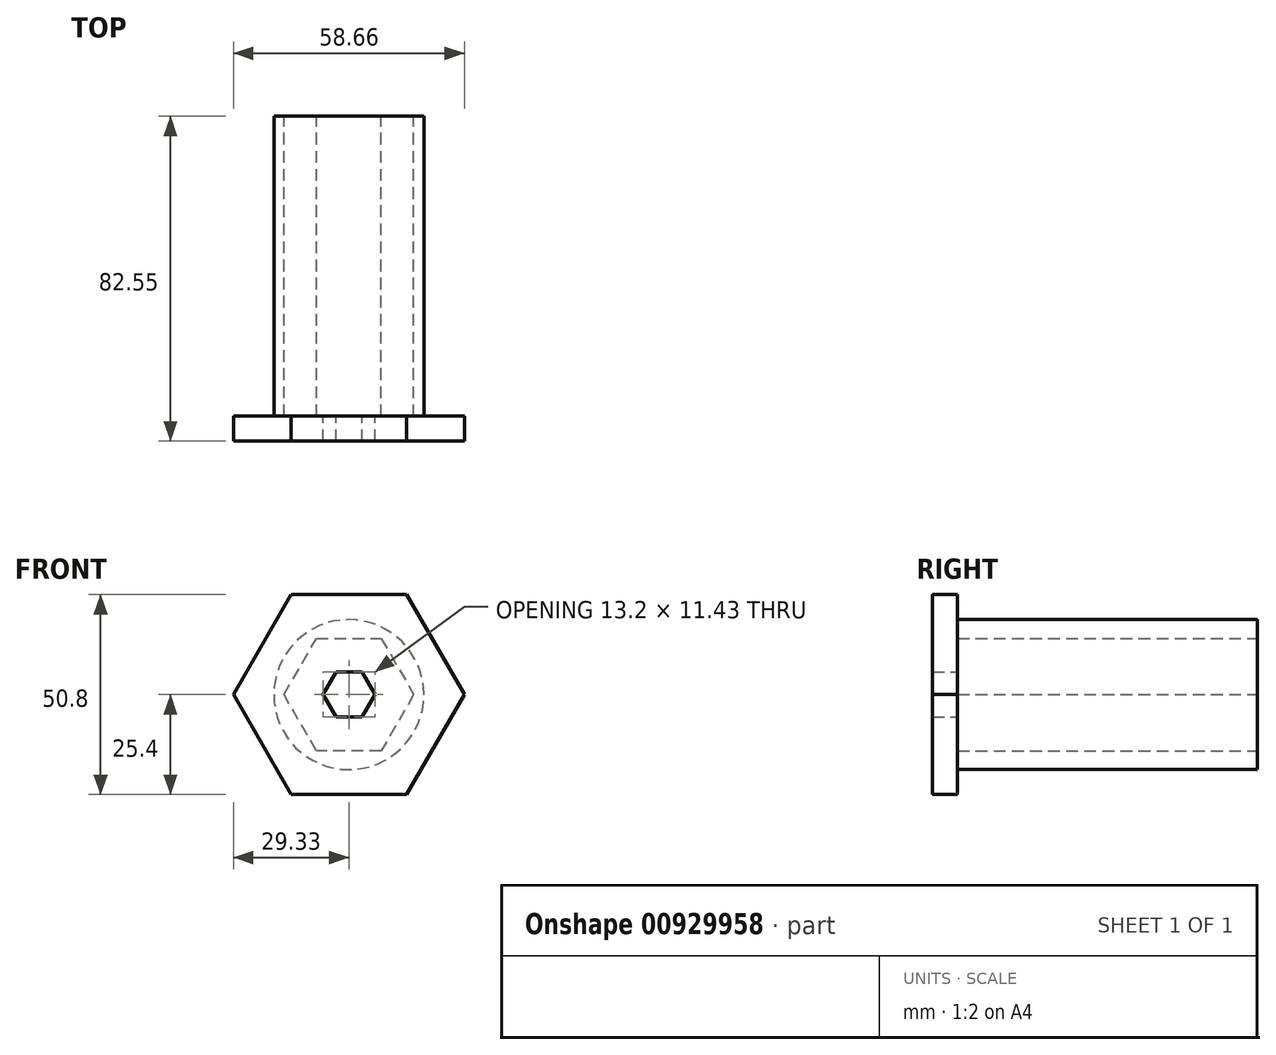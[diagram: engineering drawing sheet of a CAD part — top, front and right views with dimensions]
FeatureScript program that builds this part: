
annotation { "Feature Type Name" : "Feature", "Feature Type Description" : "" }
export const myFeature = defineFeature(function(context is Context, id is Id, definition is map)
    precondition{}
    {
        {
            var Q0;
            Q0=qCreatedBy(makeId("Front.planeOp"),FACE);
            var sketch = newSketch(context, id + "F0", { "sketchPlane" : qUnion([Q0])});
            skCircle(sketch, "E0", {"center": v(0, 0) * mm, "radius": 19.05 * mm});
            skCircle(sketch, "E1.cCircle", {"center": v(0, 0) * mm, "radius": 14.29 * mm, "construction": true});
            skLineSegment(sketch, "E1.0", {"start": v(-8.25, 14.29) * mm, "end": v(8.25, 14.29) * mm});
            skLineSegment(sketch, "E1.1", {"start": v(8.25, 14.29) * mm, "end": v(16.5, 0) * mm});
            skLineSegment(sketch, "E1.2", {"start": v(16.5, 0) * mm, "end": v(8.25, -14.29) * mm});
            skLineSegment(sketch, "E1.3", {"start": v(8.25, -14.29) * mm, "end": v(-8.25, -14.29) * mm});
            skLineSegment(sketch, "E1.4", {"start": v(-8.25, -14.29) * mm, "end": v(-16.5, 0) * mm});
            skLineSegment(sketch, "E1.5", {"start": v(-16.5, 0) * mm, "end": v(-8.25, 14.29) * mm});
            skPoint(sketch, "E1.0.midPoint", {"position": v(0, 14.29) * mm});
            skSolve(sketch);
        }
        {
            var Q0;
            Q0=makeQuery(id+"F0.imprint","IMPRINT",FACE,{"disambiguationData":[TD([[makeQuery(id+"F0.imprint","IMPRINT",EDGE,{"derivedFrom":sQuery(id+"F0.wireOp",EDGE,"E0")}),1.0]])]});
            extrude(context, id + "F1", {"entities" : qUnion([Q0]), "endBound" : BoundingType.SYMMETRIC, "depth" : 76.2 * mm, "offsetDistance" : 25.4 * mm});
        }
        {
            var Q0;
            Q0=makeQuery(id+"F1.opExtrude","CAP_FACE",FACE,{"disambiguationData":[OSD([sQuery(id+"F0.wireOp",EDGE,"E0"),sQuery(id+"F0.wireOp",EDGE,"E1.0"),sQuery(id+"F0.wireOp",EDGE,"E1.1"),sQuery(id+"F0.wireOp",EDGE,"E1.2"),sQuery(id+"F0.wireOp",EDGE,"E1.3"),sQuery(id+"F0.wireOp",EDGE,"E1.4"),sQuery(id+"F0.wireOp",EDGE,"E1.5")])],"isStart":false});
            var sketch = newSketch(context, id + "F2", { "sketchPlane" : qUnion([Q0])});
            skCircle(sketch, "E2.cCircle", {"center": v(0, 0) * mm, "radius": 25.4 * mm, "construction": true});
            skLineSegment(sketch, "E2.0", {"start": v(-14.66, 25.4) * mm, "end": v(14.66, 25.4) * mm});
            skLineSegment(sketch, "E2.1", {"start": v(14.66, 25.4) * mm, "end": v(29.33, 0) * mm});
            skLineSegment(sketch, "E2.2", {"start": v(29.33, 0) * mm, "end": v(14.66, -25.4) * mm});
            skLineSegment(sketch, "E2.3", {"start": v(14.66, -25.4) * mm, "end": v(-14.66, -25.4) * mm});
            skLineSegment(sketch, "E2.4", {"start": v(-14.66, -25.4) * mm, "end": v(-29.33, 0) * mm});
            skLineSegment(sketch, "E2.5", {"start": v(-29.33, 0) * mm, "end": v(-14.66, 25.4) * mm});
            skCircle(sketch, "E3.cCircle", {"center": v(0, 0) * mm, "radius": 5.72 * mm, "construction": true});
            skLineSegment(sketch, "E3.0", {"start": v(-3.3, 5.72) * mm, "end": v(3.3, 5.72) * mm});
            skLineSegment(sketch, "E3.1", {"start": v(3.3, 5.72) * mm, "end": v(6.6, 0) * mm});
            skLineSegment(sketch, "E3.2", {"start": v(6.6, 0) * mm, "end": v(3.3, -5.72) * mm});
            skLineSegment(sketch, "E3.3", {"start": v(3.3, -5.71) * mm, "end": v(-3.3, -5.72) * mm});
            skLineSegment(sketch, "E3.4", {"start": v(-3.3, -5.72) * mm, "end": v(-6.6, 0) * mm});
            skLineSegment(sketch, "E3.5", {"start": v(-6.6, 0) * mm, "end": v(-3.3, 5.72) * mm});
            skSolve(sketch);
        }
        {
            var Q0;
            Q0 = qSketchRegion(id + "F2", true);
            extrude(context, id + "F3", {"entities" : qUnion([Q0]), "operationType" : NewBodyOperationType.ADD, "depth" : 6.35 * mm, "offsetDistance" : 25.4 * mm});
        }
    });
